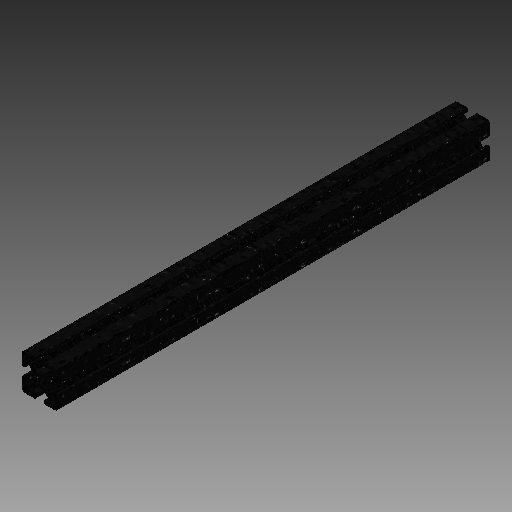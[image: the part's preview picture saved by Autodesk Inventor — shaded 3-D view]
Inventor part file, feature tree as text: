
AUTODESK INVENTOR PART (.ipt)
format: ipt  version: 2019 (Build 230136000, 136)  size: 260,608 bytes
history: native  units: in
note: dims shown in document units (in); Inventor stores cm internally (conversion verified against a paired STEP export)
features: extrude x1, sketch x1
ambient origin geometry x8: Origin, YZ Plane, XZ Plane, XY Plane, X Axis, Y Axis, Z Axis, Center Point
bodies: Solid1 (feature_tree)
feature tree (2):
  extrude  "Extrusion1"  [1 undecoded]
  sketch  "Sketch1"  dims[d0=18.0in d1=0.0in]
note: 1 required parameter value undecoded (feature->parameter linkage not recoverable at this tier; creation-order binding heuristic only, values carry confidence <= 0.55)
